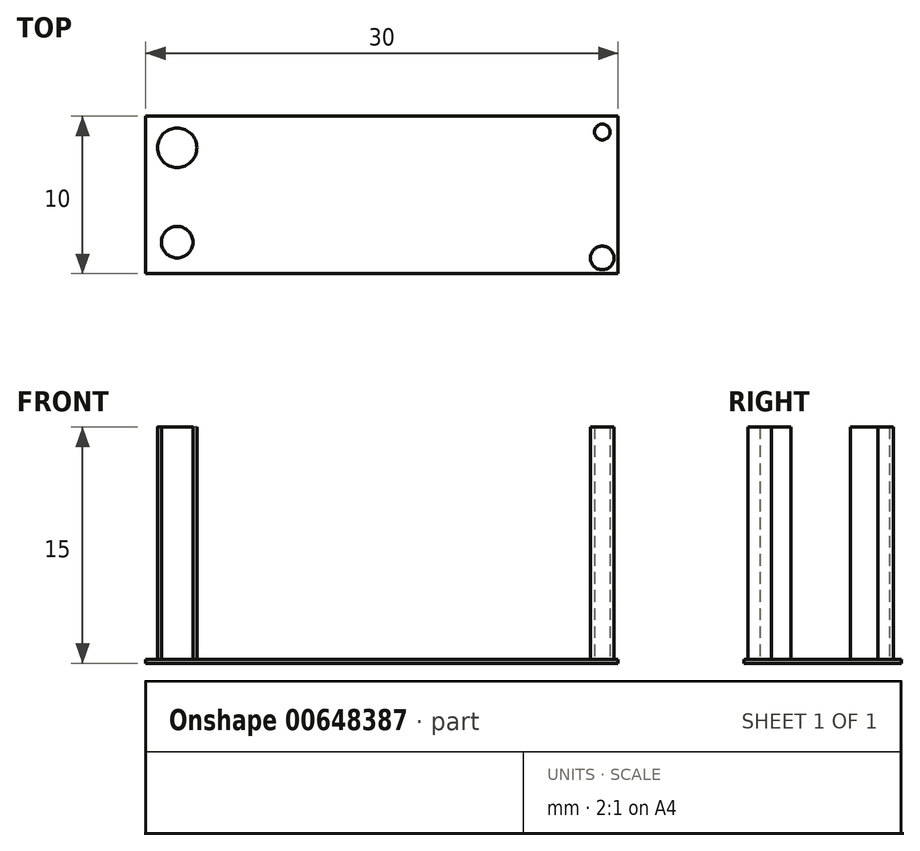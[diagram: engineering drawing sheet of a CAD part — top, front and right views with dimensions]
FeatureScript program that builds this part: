
annotation { "Feature Type Name" : "Feature", "Feature Type Description" : "" }
export const myFeature = defineFeature(function(context is Context, id is Id, definition is map)
    precondition{}
    {
        {
            var Q0;
            Q0=qCreatedBy(makeId("Top.planeOp"),FACE);
            var sketch = newSketch(context, id + "F0", { "sketchPlane" : qUnion([Q0])});
            skLineSegment(sketch, "E0.bottom", {"start": v(-15, 5.43) * mm, "end": v(15, 5.43) * mm});
            skLineSegment(sketch, "E0.top", {"start": v(-15, -4.57) * mm, "end": v(15, -4.57) * mm});
            skLineSegment(sketch, "E0.left", {"start": v(-15, 5.43) * mm, "end": v(-15, -4.57) * mm});
            skLineSegment(sketch, "E0.right", {"start": v(15, 5.43) * mm, "end": v(15, -4.57) * mm});
            skCircle(sketch, "E1", {"center": v(-13, 3.43) * mm, "radius": 1.25 * mm});
            skCircle(sketch, "E2", {"center": v(-13, -2.57) * mm, "radius": 1 * mm});
            skCircle(sketch, "E3", {"center": v(14, -3.57) * mm, "radius": 0.75 * mm});
            skCircle(sketch, "E4", {"center": v(14, 4.43) * mm, "radius": 0.5 * mm});
            skSolve(sketch);
        }
        {
            var Q0;
            Q0=makeQuery(id+"F0.imprint","IMPRINT",FACE,{"disambiguationData":[TD([[makeQuery(id+"F0.imprint","IMPRINT",EDGE,{"derivedFrom":sQuery(id+"F0.wireOp",EDGE,"E0.bottom")}),-1.0]])]});
            extrude(context, id + "F1", {"entities" : qUnion([Q0]), "depth" : .25 * mm, "offsetDistance" : 25 * mm});
        }
        {
            var Q0;
            Q0=makeQuery(id+"F0.imprint","IMPRINT",FACE,{"disambiguationData":[TD([[makeQuery(id+"F0.imprint","IMPRINT",EDGE,{"derivedFrom":sQuery(id+"F0.wireOp",EDGE,"E1")}),1.0]])]});
            var Q1;
            Q1=makeQuery(id+"F0.imprint","IMPRINT",FACE,{"disambiguationData":[TD([[makeQuery(id+"F0.imprint","IMPRINT",EDGE,{"derivedFrom":sQuery(id+"F0.wireOp",EDGE,"E2")}),1.0]])]});
            var Q2;
            Q2=makeQuery(id+"F0.imprint","IMPRINT",FACE,{"disambiguationData":[TD([[makeQuery(id+"F0.imprint","IMPRINT",EDGE,{"derivedFrom":sQuery(id+"F0.wireOp",EDGE,"E3")}),1.0]])]});
            var Q3;
            Q3=makeQuery(id+"F0.imprint","IMPRINT",FACE,{"disambiguationData":[TD([[makeQuery(id+"F0.imprint","IMPRINT",EDGE,{"derivedFrom":sQuery(id+"F0.wireOp",EDGE,"E4")}),1.0]])]});
            extrude(context, id + "F2", {"entities" : qUnion([Q0, Q1, Q2, Q3]), "operationType" : NewBodyOperationType.ADD, "depth" : 15 * mm, "offsetDistance" : 25 * mm});
        }
    });
